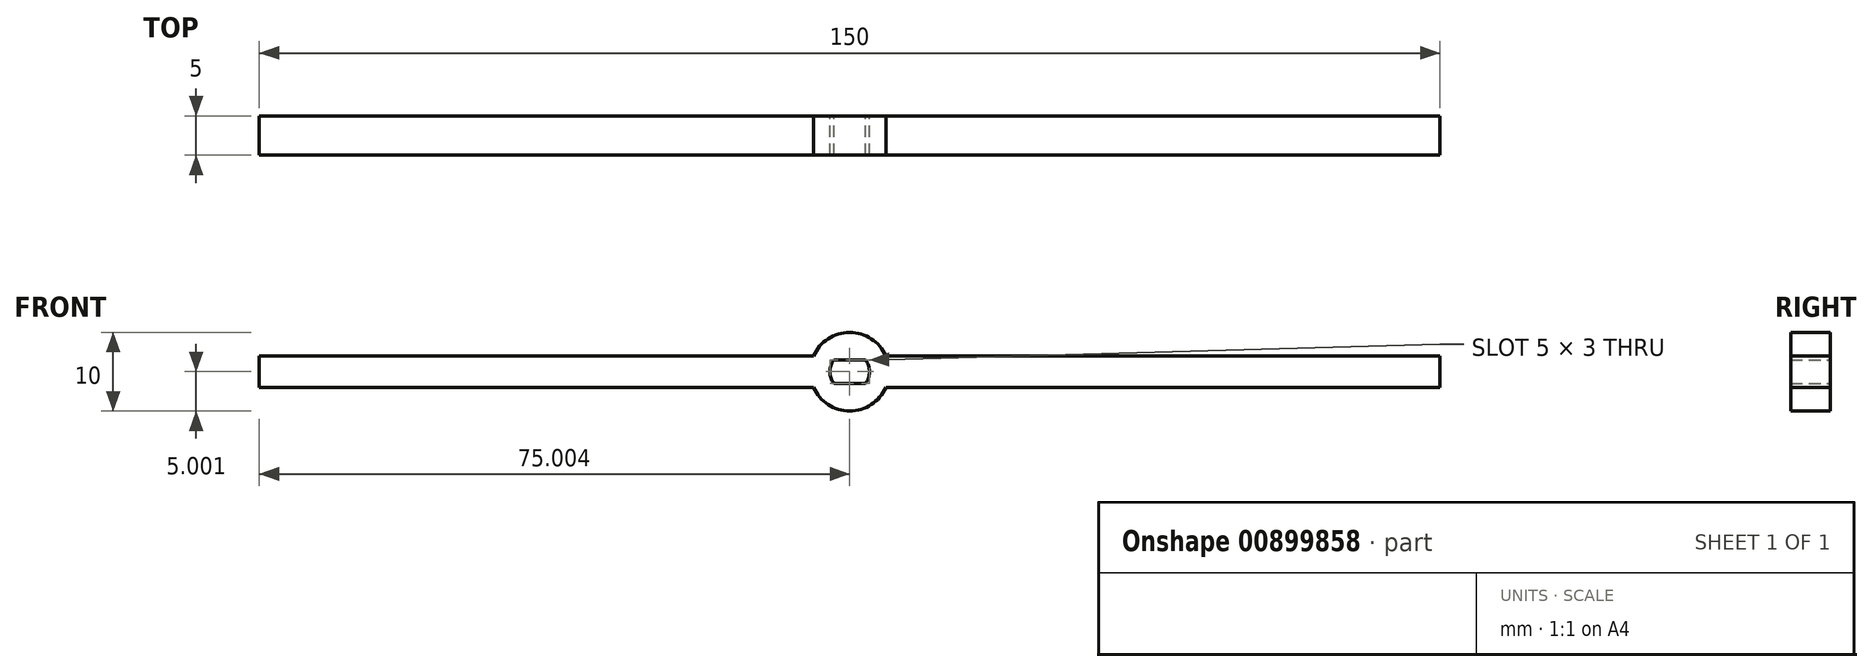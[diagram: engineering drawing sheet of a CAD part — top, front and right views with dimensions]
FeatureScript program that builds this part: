
annotation { "Feature Type Name" : "Feature", "Feature Type Description" : "" }
export const myFeature = defineFeature(function(context is Context, id is Id, definition is map)
    precondition{}
    {
        {
            var Q0;
            Q0=qCreatedBy(makeId("Front.planeOp"),FACE);
            var sketch = newSketch(context, id + "F0", { "sketchPlane" : qUnion([Q0])});
            skLineSegment(sketch, "E0.bottom", {"start": v(15.03, 35.76) * mm, "end": v(-55.38, 35.76) * mm});
            skLineSegment(sketch, "E0.top", {"start": v(15.03, 39.76) * mm, "end": v(-55.38, 39.76) * mm});
            skLineSegment(sketch, "E0.left", {"start": v(15.03, 35.76) * mm, "end": v(15.03, 39.76) * mm});
            skLineSegment(sketch, "E0.right", {"start": v(-134.97, 35.76) * mm, "end": v(-134.97, 39.76) * mm});
            skArc(sketch, "E1", {"start": v(-64.55, 35.76) * mm, "mid": v(-59.97, 32.76) * mm, "end": v(-55.38, 35.76) * mm});
            skLineSegment(sketch, "E2.trimOffspring", {"start": v(-64.55, 39.76) * mm, "end": v(-134.97, 39.76) * mm});
            skLineSegment(sketch, "E3.trimOffspring", {"start": v(-64.55, 35.76) * mm, "end": v(-134.97, 35.76) * mm});
            skArc(sketch, "E4.trimOffspring", {"start": v(-55.38, 39.76) * mm, "mid": v(-59.97, 42.76) * mm, "end": v(-64.55, 39.76) * mm});
            skArc(sketch, "E5", {"start": v(-61.97, 39.26) * mm, "mid": v(-62.47, 37.76) * mm, "end": v(-61.97, 36.26) * mm});
            skLineSegment(sketch, "E6.bottom", {"start": v(-57.97, 36.26) * mm, "end": v(-61.97, 36.26) * mm});
            skLineSegment(sketch, "E6.top", {"start": v(-57.97, 39.26) * mm, "end": v(-61.97, 39.26) * mm});
            skArc(sketch, "E7.trimOffspring", {"start": v(-57.97, 36.26) * mm, "mid": v(-57.47, 37.76) * mm, "end": v(-57.97, 39.26) * mm});
            skSolve(sketch);
        }
        {
            var Q0;
            Q0 = qSketchRegion(id + "F0", true);
            extrude(context, id + "F1", {"entities" : qUnion([Q0]), "depth" : 5 * mm, "offsetDistance" : 25 * mm});
        }
    });
